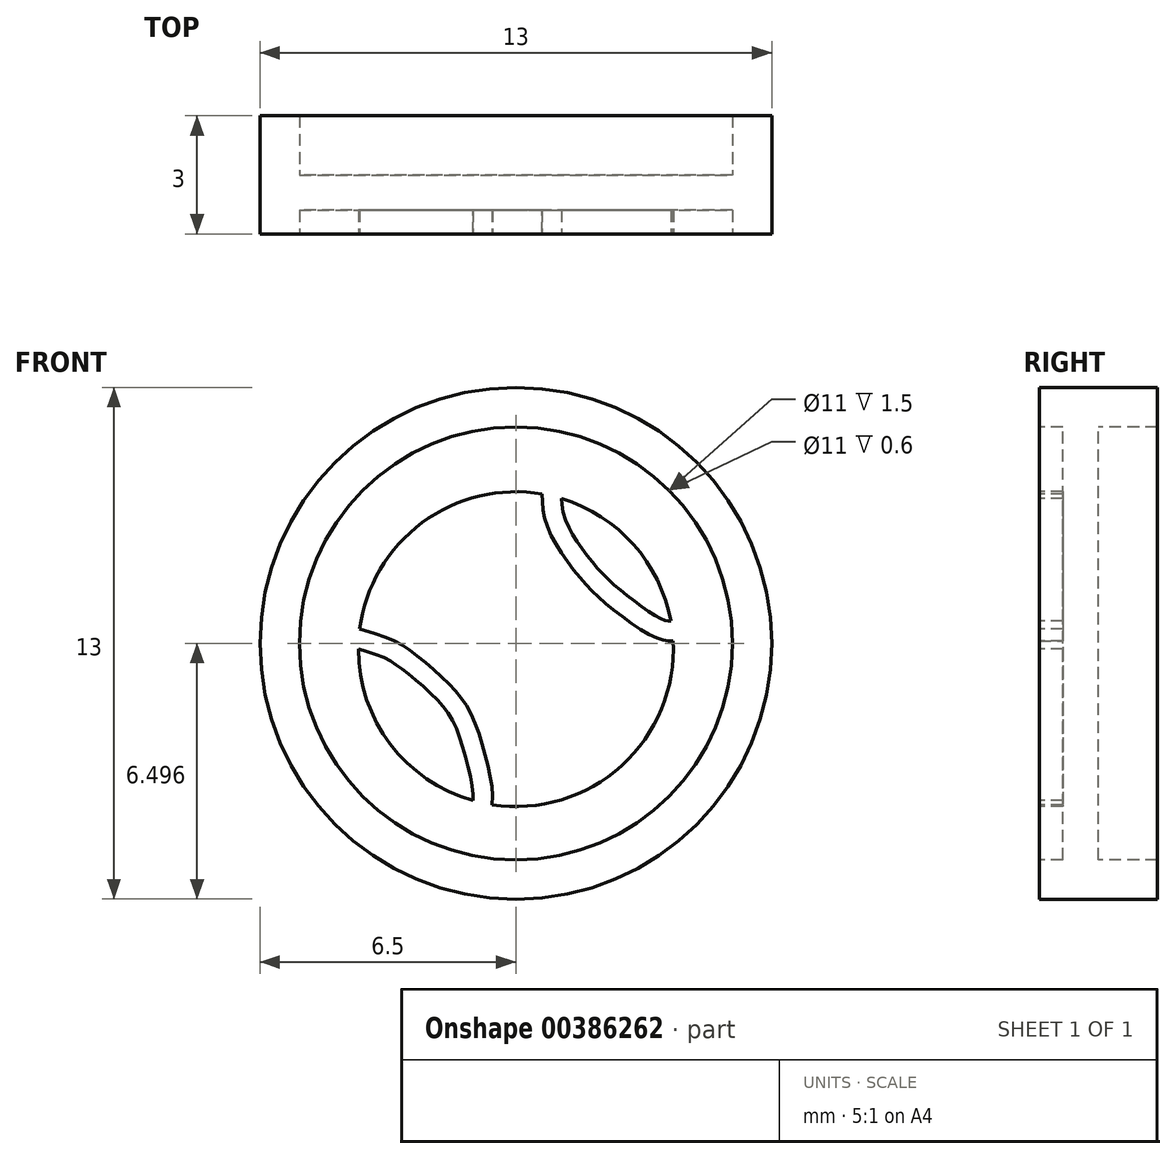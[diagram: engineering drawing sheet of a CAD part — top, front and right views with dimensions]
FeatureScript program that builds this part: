
annotation { "Feature Type Name" : "Feature", "Feature Type Description" : "" }
export const myFeature = defineFeature(function(context is Context, id is Id, definition is map)
    precondition{}
    {
        {
            var Q0;
            Q0=qCreatedBy(makeId("Front.planeOp"),FACE);
            var sketch = newSketch(context, id + "F0", { "sketchPlane" : qUnion([Q0])});
            skFitSpline(sketch, "E0", {"points": [v(-1.46, -3.84) * mm, v(1.4, -3.82) * mm, v(2.08, -2.53) * mm, v(2.16, -0.81) * mm, v(2.04, 0.87) * mm, v(1.96, 1.38) * mm, v(2.08, 1.44) * mm, v(2.08, 1.56) * mm, v(1.91, 1.69) * mm, v(1.9, 2) * mm, v(1.81, 2.4) * mm, v(1.5, 2.63) * mm, v(1.3, 2.93) * mm, v(0.95, 3.1) * mm, v(0.65, 3.2) * mm, v(0.5, 3.4) * mm, v(0.56, 3.81) * mm, v(0.36, 4.2) * mm, v(0, 4.29) * mm, v(-0.3, 4.2) * mm, v(-0.56, 3.94) * mm, v(-0.54, 3.61) * mm, v(-0.48, 3.36) * mm, v(-0.69, 3.16) * mm, v(-1, 3.08) * mm, v(-1.22, 2.91) * mm, v(-1.36, 2.83) * mm, v(-1.42, 2.69) * mm, v(-1.65, 2.67) * mm, v(-1.81, 2.34) * mm, v(-1.85, 2) * mm, v(-1.91, 1.73) * mm, v(-2.08, 1.58) * mm, v(-2.06, 1.44) * mm, v(-1.98, 1.42) * mm, v(-2.06, 0.95) * mm, v(-2.12, 0.21) * mm, v(-2.18, -0.5) * mm, v(-2.18, -1.22) * mm, v(-2.12, -2.55) * mm, v(-1.9, -3.41) * mm, v(-1.46, -3.84) * mm]});
            skSolve(sketch);
        }
        {
            var Q0;
            Q0=qCreatedBy(makeId("Front.planeOp"),FACE);
            var sketch = newSketch(context, id + "F1", { "sketchPlane" : qUnion([Q0])});
            skCircle(sketch, "E1", {"center": v(0, 0.15) * mm, "radius": 6.5 * mm});
            skCircle(sketch, "E2.0", {"center": v(0, 0.15) * mm, "radius": 5.5 * mm});
            skSolve(sketch);
        }
        {
            var Q0;
            Q0=makeQuery(id+"F1.imprint","IMPRINT",FACE,{"disambiguationData":[TD([[makeQuery(id+"F1.imprint","IMPRINT",EDGE,{"derivedFrom":sQuery(id+"F1.wireOp",EDGE,"E2.0")}),1.0]])]});
            var sketch = newSketch(context, id + "F2", { "sketchPlane" : qUnion([Q0])});
            skCircle(sketch, "E3", {"center": v(0, 0) * mm, "radius": 4 * mm});
            skFitSpline(sketch, "E4", {"points": [v(-3.97, 0.51) * mm, v(-2.74, 0) * mm, v(-1.8, -0.8) * mm, v(-1.17, -1.58) * mm, v(-0.74, -2.84) * mm, v(-0.6, -3.95) * mm], "startDerivative": vector(10.12, -2.9) * mm, "endDerivative": vector(-0.63, -4.94) * mm});
            skFitSpline(sketch, "E5.0", {"points": [v(-4.1, 0.03) * mm, v(-3.9, -0.03) * mm, v(-3.58, -0.13) * mm, v(-3.3, -0.24) * mm, v(-3.15, -0.32) * mm, v(-3, -0.43) * mm, v(-2.82, -0.56) * mm, v(-2.58, -0.75) * mm, v(-2.3, -1) * mm, v(-2.04, -1.25) * mm, v(-1.84, -1.46) * mm, v(-1.68, -1.68) * mm, v(-1.55, -1.92) * mm, v(-1.43, -2.25) * mm, v(-1.31, -2.61) * mm, v(-1.21, -3) * mm, v(-1.13, -3.36) * mm, v(-1.09, -3.68) * mm, v(-1.09, -3.83) * mm, v(-1.1, -3.9) * mm]});
            skFitSpline(sketch, "E6", {"points": [v(0.67, 3.94) * mm, v(0.83, 3.03) * mm, v(1.6, 1.86) * mm, v(2.42, 1.05) * mm, v(3.6, 0.27) * mm, v(4, 0.21) * mm], "startDerivative": vector(-0.18, -4.5) * mm, "endDerivative": vector(2.54, 0.21) * mm});
            skFitSpline(sketch, "E7.0", {"points": [v(1.17, 3.92) * mm, v(1.16, 3.78) * mm, v(1.18, 3.56) * mm, v(1.28, 3.24) * mm, v(1.41, 2.97) * mm, v(1.6, 2.68) * mm, v(1.8, 2.4) * mm, v(2.02, 2.13) * mm, v(2.22, 1.9) * mm, v(2.43, 1.7) * mm, v(2.66, 1.5) * mm, v(2.96, 1.26) * mm, v(3.28, 1.02) * mm, v(3.53, 0.86) * mm, v(3.7, 0.77) * mm, v(3.79, 0.73) * mm, v(3.84, 0.72) * mm, v(3.89, 0.7) * mm, v(3.92, 0.7) * mm, v(3.95, 0.71) * mm]});
            skSolve(sketch);
        }
        {
            var Q0;
            Q0 = qSketchRegion(id + "F1", true);
            extrude(context, id + "F3", {"entities" : qUnion([Q0]), "oppositeDirection" : true, "depth" : 3 * mm});
        }
        {
            var Q0;
            Q0 = qSketchRegion(id + "F0", true);
            var Q1;
            Q1=makeQuery(id+"F1.imprint","IMPRINT",FACE,{"disambiguationData":[TD([[makeQuery(id+"F1.imprint","IMPRINT",EDGE,{"derivedFrom":sQuery(id+"F1.wireOp",EDGE,"E2.0")}),1.0]])]});
            extrude(context, id + "F4", {"entities" : qUnion([Q0, Q1]), "operationType" : NewBodyOperationType.ADD, "oppositeDirection" : true, "depth" : 1.5 * mm});
        }
        {
            var Q0;
            Q0=makeQuery(id+"F1.imprint","IMPRINT",FACE,{"disambiguationData":[TD([[makeQuery(id+"F1.imprint","IMPRINT",EDGE,{"derivedFrom":sQuery(id+"F1.wireOp",EDGE,"E2.0")}),1.0]])]});
            var Q1;
            Q1 = qSketchRegion(id + "F0", true);
            extrude(context, id + "F5", {"entities" : qUnion([Q0, Q1]), "operationType" : NewBodyOperationType.REMOVE, "oppositeDirection" : true, "depth" : .6 * mm});
        }
        {
            var Q0;
            {var subQ0=sQuery(id+"F2.wireOp",EDGE,"E4");Q0=makeQuery(id+"F2.imprint","IMPRINT",FACE,{"disambiguationData":[TD([[makeQuery(id+"F2.imprint","IMPRINT",EDGE,{"derivedFrom":subQ0}),1.0]])]});}
            extrude(context, id + "F6", {"entities" : qUnion([Q0]), "operationType" : NewBodyOperationType.ADD, "oppositeDirection" : true, "depth" : 1 * mm});
        }
        {
            var Q0;
            {var subQ0=sQuery(id+"F2.wireOp",EDGE,"E5.0");Q0=makeQuery(id+"F2.imprint","IMPRINT",FACE,{"disambiguationData":[TD([[makeQuery(id+"F2.imprint","IMPRINT",EDGE,{"derivedFrom":subQ0}),-1.0]])]});}
            extrude(context, id + "F7", {"entities" : qUnion([Q0]), "operationType" : NewBodyOperationType.ADD, "oppositeDirection" : true, "depth" : 1 * mm});
        }
        {
            var Q0;
            {var subQ0=sQuery(id+"F2.wireOp",EDGE,"E7.0");Q0=makeQuery(id+"F2.imprint","IMPRINT",FACE,{"disambiguationData":[TD([[makeQuery(id+"F2.imprint","IMPRINT",EDGE,{"derivedFrom":subQ0}),1.0]])]});}
            extrude(context, id + "F8", {"entities" : qUnion([Q0]), "operationType" : NewBodyOperationType.ADD, "oppositeDirection" : true, "depth" : 1 * mm});
        }
    });
